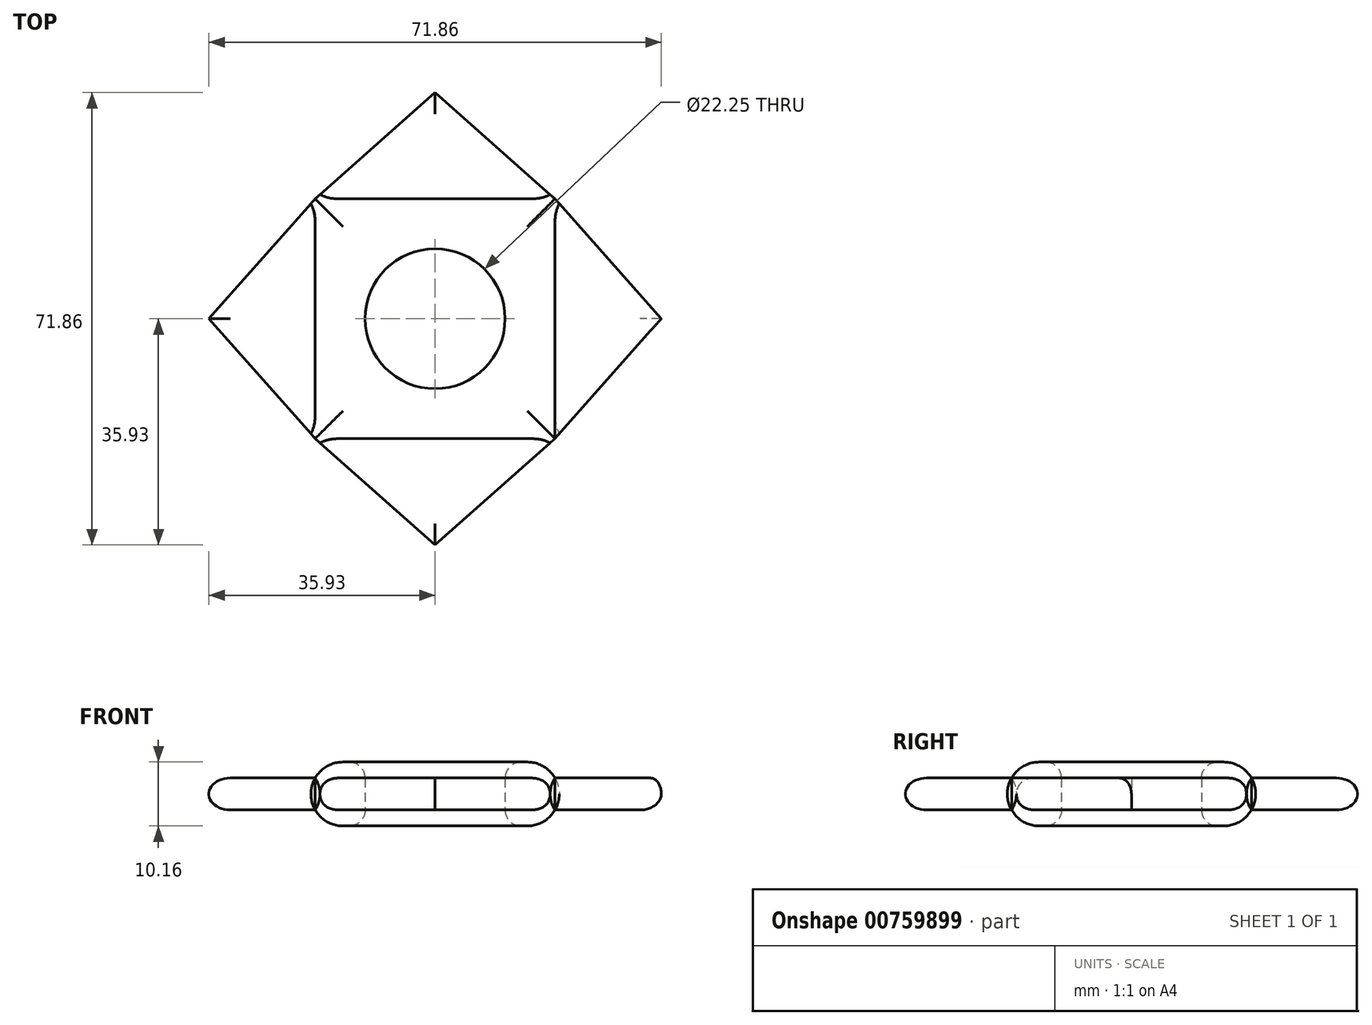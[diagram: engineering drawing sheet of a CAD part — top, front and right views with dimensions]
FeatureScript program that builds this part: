
annotation { "Feature Type Name" : "Feature", "Feature Type Description" : "" }
export const myFeature = defineFeature(function(context is Context, id is Id, definition is map)
    precondition{}
    {
        {
            var Q0;
            Q0=qCreatedBy(makeId("Top.planeOp"),FACE);
            var sketch = newSketch(context, id + "F0", { "sketchPlane" : qUnion([Q0])});
            skLineSegment(sketch, "E0.bottom", {"start": v(-19.05, 19.05) * mm, "end": v(19.05, 19.05) * mm});
            skLineSegment(sketch, "E0.top", {"start": v(-19.05, -19.05) * mm, "end": v(19.05, -19.05) * mm});
            skLineSegment(sketch, "E0.left", {"start": v(-19.05, 19.05) * mm, "end": v(-19.05, -19.05) * mm});
            skLineSegment(sketch, "E0.right", {"start": v(19.05, 19.05) * mm, "end": v(19.05, -19.05) * mm});
            skPoint(sketch, "E0.middle", {"position": v(0, 0) * mm});
            skCircle(sketch, "E1", {"center": v(0, 0) * mm, "radius": 11.13 * mm});
            skPoint(sketch, "E2.endSnap0", {"position": v(0, 19.05) * mm});
            skPoint(sketch, "E3.endSnap0", {"position": v(-19.05, 0) * mm});
            skLineSegment(sketch, "E4", {"start": v(-19.05, 19.05) * mm, "end": v(0, 35.93) * mm});
            skLineSegment(sketch, "E5", {"start": v(0, 35.93) * mm, "end": v(19.05, 19.05) * mm});
            skLineSegment(sketch, "E6", {"start": v(19.05, 19.05) * mm, "end": v(35.93, 0) * mm});
            skLineSegment(sketch, "E7", {"start": v(35.93, 0) * mm, "end": v(19.05, -19.05) * mm});
            skLineSegment(sketch, "E8", {"start": v(19.05, -19.05) * mm, "end": v(0, -35.93) * mm});
            skLineSegment(sketch, "E9", {"start": v(0, -35.93) * mm, "end": v(-19.05, -19.05) * mm});
            skLineSegment(sketch, "E10", {"start": v(-19.05, -19.05) * mm, "end": v(-35.93, 0) * mm});
            skLineSegment(sketch, "E11", {"start": v(-35.93, 0) * mm, "end": v(-19.05, 19.05) * mm});
            skSolve(sketch);
        }
        {
            var Q0;
            Q0=makeQuery(id+"F0.imprint","IMPRINT",FACE,{"disambiguationData":[TD([[makeQuery(id+"F0.imprint","IMPRINT",EDGE,{"derivedFrom":sQuery(id+"F0.wireOp",EDGE,"E0.bottom")}),-1.0]])]});
            extrude(context, id + "F1", {"entities" : qUnion([Q0]), "endBound" : BoundingType.SYMMETRIC, "depth" : 10.16 * mm, "offsetDistance" : 25.4 * mm});
        }
        {
            var Q0;
            Q0=makeQuery(id+"F0.imprint","IMPRINT",FACE,{"disambiguationData":[TD([[makeQuery(id+"F0.imprint","IMPRINT",EDGE,{"derivedFrom":sQuery(id+"F0.wireOp",EDGE,"E0.left")}),-1.0]])]});
            var Q1;
            Q1=makeQuery(id+"F0.imprint","IMPRINT",FACE,{"disambiguationData":[TD([[makeQuery(id+"F0.imprint","IMPRINT",EDGE,{"derivedFrom":sQuery(id+"F0.wireOp",EDGE,"E0.top")}),-1.0]])]});
            var Q2;
            Q2=makeQuery(id+"F0.imprint","IMPRINT",FACE,{"disambiguationData":[TD([[makeQuery(id+"F0.imprint","IMPRINT",EDGE,{"derivedFrom":sQuery(id+"F0.wireOp",EDGE,"E0.right")}),1.0]])]});
            var Q3;
            Q3=makeQuery(id+"F0.imprint","IMPRINT",FACE,{"disambiguationData":[TD([[makeQuery(id+"F0.imprint","IMPRINT",EDGE,{"derivedFrom":sQuery(id+"F0.wireOp",EDGE,"E0.bottom")}),1.0]])]});
            extrude(context, id + "F2", {"entities" : qUnion([Q0, Q1, Q2, Q3]), "operationType" : NewBodyOperationType.ADD, "endBound" : BoundingType.SYMMETRIC, "depth" : 5.08 * mm, "offsetDistance" : 25.4 * mm});
        }
        {
            var Q0;
            Q0=makeQuery(id+"F1.opExtrude","CAP_EDGE",EDGE,{"disambiguationData":[OSD([sQuery(id+"F0.wireOp",EDGE,"E1")])],"isStart":false});
            var Q1;
            Q1=makeQuery(id+"F1.opExtrude","CAP_EDGE",EDGE,{"disambiguationData":[OSD([sQuery(id+"F0.wireOp",EDGE,"E1")])],"isStart":true});
            fillet(context, id + "F3", {"entities" : qUnion([Q0, Q1]), "radius" : 2.54 * mm, "tangentPropagation" : true, "allowEdgeOverflow" : false});
        }
        {
            var Q0;
            Q0=makeQuery(id+"F1.opExtrude","CAP_EDGE",EDGE,{"disambiguationData":[OSD([sQuery(id+"F0.wireOp",EDGE,"E0.left")])],"isStart":false});
            var Q1;
            Q1=makeQuery(id+"F1.opExtrude","CAP_EDGE",EDGE,{"disambiguationData":[OSD([sQuery(id+"F0.wireOp",EDGE,"E0.bottom")])],"isStart":false});
            var Q2;
            Q2=makeQuery(id+"F1.opExtrude","CAP_EDGE",EDGE,{"disambiguationData":[OSD([sQuery(id+"F0.wireOp",EDGE,"E0.right")])],"isStart":false});
            var Q3;
            Q3=makeQuery(id+"F1.opExtrude","CAP_EDGE",EDGE,{"disambiguationData":[OSD([sQuery(id+"F0.wireOp",EDGE,"E0.top")])],"isStart":false});
            var Q4;
            Q4=makeQuery(id+"F1.opExtrude","CAP_EDGE",EDGE,{"disambiguationData":[OSD([sQuery(id+"F0.wireOp",EDGE,"E0.top")])],"isStart":true});
            var Q5;
            Q5=makeQuery(id+"F1.opExtrude","CAP_EDGE",EDGE,{"disambiguationData":[OSD([sQuery(id+"F0.wireOp",EDGE,"E0.right")])],"isStart":true});
            var Q6;
            Q6=makeQuery(id+"F1.opExtrude","CAP_EDGE",EDGE,{"disambiguationData":[OSD([sQuery(id+"F0.wireOp",EDGE,"E0.bottom")])],"isStart":true});
            var Q7;
            Q7=makeQuery(id+"F1.opExtrude","CAP_EDGE",EDGE,{"disambiguationData":[OSD([sQuery(id+"F0.wireOp",EDGE,"E0.left")])],"isStart":true});
            fillet(context, id + "F4", {"entities" : qUnion([Q0, Q1, Q2, Q3, Q4, Q5, Q6, Q7]), "radius" : 5.08 * mm, "tangentPropagation" : true, "allowEdgeOverflow" : false});
        }
        {
            var Q0;
            Q0=makeQuery(id+"F2.opExtrude","CAP_EDGE",EDGE,{"disambiguationData":[OSD([sQuery(id+"F0.wireOp",EDGE,"E11")])],"isStart":true});
            var Q1;
            Q1=makeQuery(id+"F2.opExtrude","CAP_EDGE",EDGE,{"disambiguationData":[OSD([sQuery(id+"F0.wireOp",EDGE,"E4")])],"isStart":true});
            var Q2;
            Q2=makeQuery(id+"F2.opExtrude","CAP_EDGE",EDGE,{"disambiguationData":[OSD([sQuery(id+"F0.wireOp",EDGE,"E10")])],"isStart":true});
            var Q3;
            Q3=makeQuery(id+"F2.opExtrude","CAP_EDGE",EDGE,{"disambiguationData":[OSD([sQuery(id+"F0.wireOp",EDGE,"E9")])],"isStart":true});
            var Q4;
            Q4=makeQuery(id+"F2.opExtrude","CAP_EDGE",EDGE,{"disambiguationData":[OSD([sQuery(id+"F0.wireOp",EDGE,"E8")])],"isStart":true});
            var Q5;
            Q5=makeQuery(id+"F2.opExtrude","CAP_EDGE",EDGE,{"disambiguationData":[OSD([sQuery(id+"F0.wireOp",EDGE,"E7")])],"isStart":true});
            var Q6;
            Q6=makeQuery(id+"F2.opExtrude","CAP_EDGE",EDGE,{"disambiguationData":[OSD([sQuery(id+"F0.wireOp",EDGE,"E6")])],"isStart":true});
            var Q7;
            Q7=makeQuery(id+"F2.opExtrude","CAP_EDGE",EDGE,{"disambiguationData":[OSD([sQuery(id+"F0.wireOp",EDGE,"E5")])],"isStart":true});
            var Q8;
            Q8=makeQuery(id+"F2.opExtrude","CAP_EDGE",EDGE,{"disambiguationData":[OSD([sQuery(id+"F0.wireOp",EDGE,"E5")])],"isStart":false});
            var Q9;
            Q9=makeQuery(id+"F2.opExtrude","CAP_EDGE",EDGE,{"disambiguationData":[OSD([sQuery(id+"F0.wireOp",EDGE,"E6")])],"isStart":false});
            var Q10;
            Q10=makeQuery(id+"F2.opExtrude","CAP_EDGE",EDGE,{"disambiguationData":[OSD([sQuery(id+"F0.wireOp",EDGE,"E4")])],"isStart":false});
            var Q11;
            Q11=makeQuery(id+"F2.opExtrude","CAP_EDGE",EDGE,{"disambiguationData":[OSD([sQuery(id+"F0.wireOp",EDGE,"E11")])],"isStart":false});
            var Q12;
            Q12=makeQuery(id+"F2.opExtrude","CAP_EDGE",EDGE,{"disambiguationData":[OSD([sQuery(id+"F0.wireOp",EDGE,"E10")])],"isStart":false});
            var Q13;
            Q13=makeQuery(id+"F2.opExtrude","CAP_EDGE",EDGE,{"disambiguationData":[OSD([sQuery(id+"F0.wireOp",EDGE,"E9")])],"isStart":false});
            var Q14;
            Q14=makeQuery(id+"F2.opExtrude","CAP_EDGE",EDGE,{"disambiguationData":[OSD([sQuery(id+"F0.wireOp",EDGE,"E8")])],"isStart":false});
            fillet(context, id + "F5", {"entities" : qUnion([Q0, Q1, Q2, Q3, Q4, Q5, Q6, Q7, Q8, Q9, Q10, Q11, Q12, Q13, Q14]), "radius" : 2.54 * mm, "tangentPropagation" : true, "allowEdgeOverflow" : false});
        }
    });
